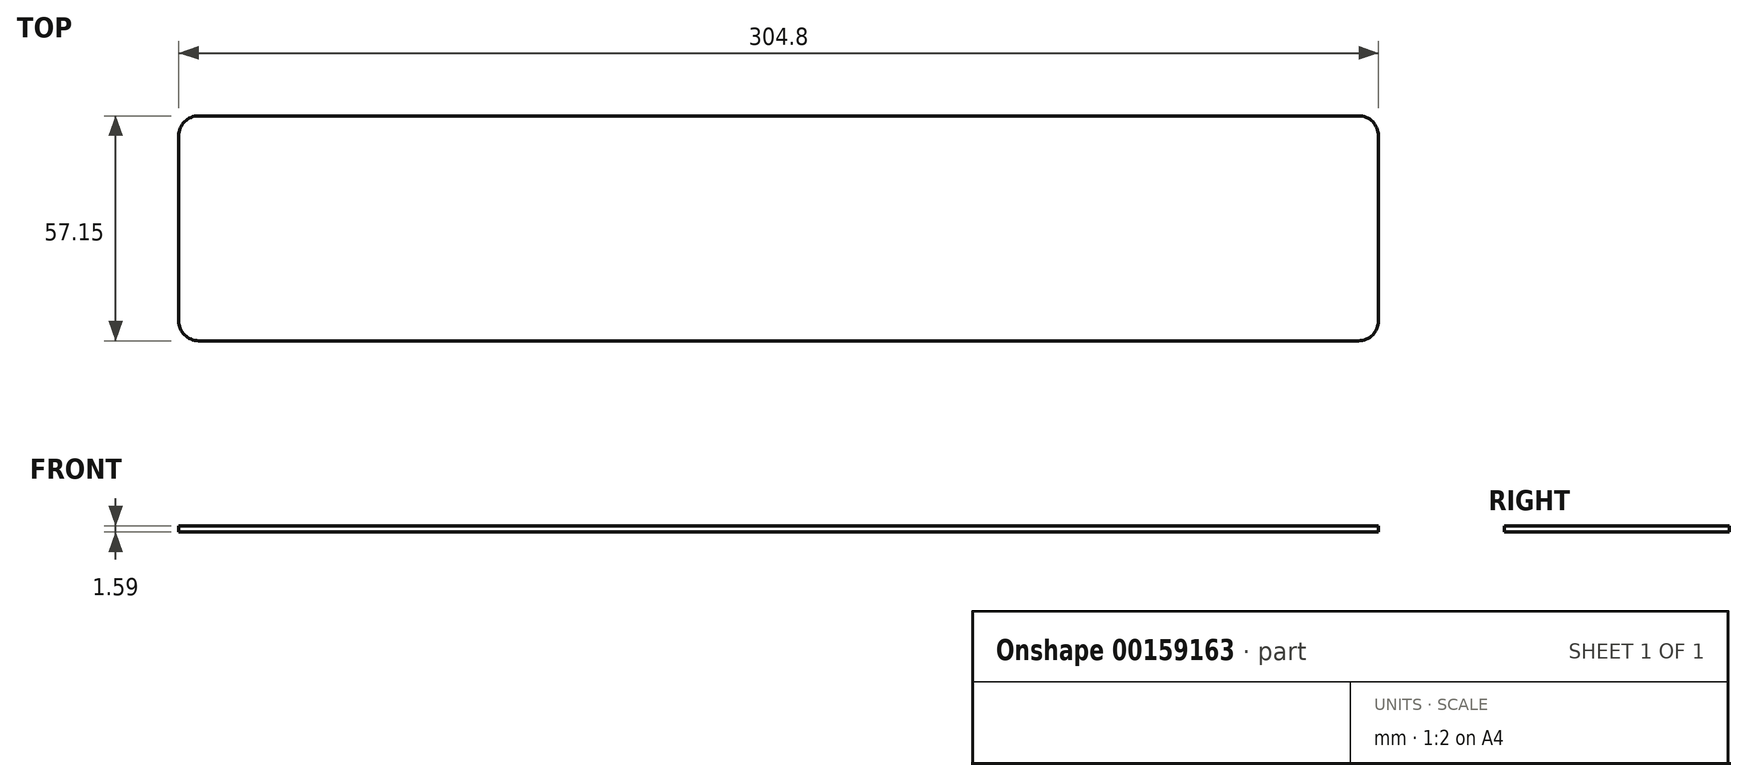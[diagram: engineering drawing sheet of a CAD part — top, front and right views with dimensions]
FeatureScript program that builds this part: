
annotation { "Feature Type Name" : "Feature", "Feature Type Description" : "" }
export const myFeature = defineFeature(function(context is Context, id is Id, definition is map)
    precondition{}
    {
        {
            var Q0;
            Q0=qCreatedBy(makeId("Top.planeOp"),FACE);
            var sketch = newSketch(context, id + "F0", { "sketchPlane" : qUnion([Q0])});
            skLineSegment(sketch, "E0.bottom", {"start": v(-99.17, -29.89) * mm, "end": v(205.63, -29.89) * mm});
            skLineSegment(sketch, "E0.top", {"start": v(-99.17, -87.04) * mm, "end": v(205.63, -87.04) * mm});
            skLineSegment(sketch, "E0.left", {"start": v(-99.17, -29.89) * mm, "end": v(-99.17, -87.04) * mm});
            skLineSegment(sketch, "E0.right", {"start": v(205.63, -29.89) * mm, "end": v(205.63, -87.04) * mm});
            skPoint(sketch, "E0.middle", {"position": v(53.23, -58.46) * mm});
            skSolve(sketch);
        }
        {
            var Q0;
            Q0 = qSketchRegion(id + "F0", true);
            extrude(context, id + "F1", {"entities" : qUnion([Q0]), "depth" : 1.59 * mm});
        }
        {
            var Q0;
            Q0=makeQuery(id+"F1.opExtrude","SWEPT_EDGE",EDGE,{"disambiguationData":[OSD([sQuery(id+"F0.wireOp",EDGE,"E0.top"),sQuery(id+"F0.wireOp",EDGE,"E0.left")])]});
            var Q1;
            Q1=makeQuery(id+"F1.opExtrude","SWEPT_EDGE",EDGE,{"disambiguationData":[OSD([sQuery(id+"F0.wireOp",EDGE,"E0.bottom"),sQuery(id+"F0.wireOp",EDGE,"E0.left")])]});
            var Q2;
            Q2=makeQuery(id+"F1.opExtrude","SWEPT_EDGE",EDGE,{"disambiguationData":[OSD([sQuery(id+"F0.wireOp",EDGE,"E0.bottom"),sQuery(id+"F0.wireOp",EDGE,"E0.right")])]});
            var Q3;
            Q3=makeQuery(id+"F1.opExtrude","SWEPT_EDGE",EDGE,{"disambiguationData":[OSD([sQuery(id+"F0.wireOp",EDGE,"E0.top"),sQuery(id+"F0.wireOp",EDGE,"E0.right")])]});
            fillet(context, id + "F2", {"entities" : qUnion([Q0, Q1, Q2, Q3]), "radius" : 5.08 * mm, "tangentPropagation" : true, "allowEdgeOverflow" : false});
        }
    });
